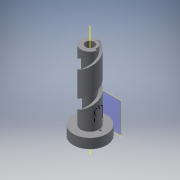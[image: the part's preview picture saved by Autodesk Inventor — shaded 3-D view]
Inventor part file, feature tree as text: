
AUTODESK INVENTOR PART (.ipt)
format: ipt  version: 2018 (Build 220112000, 112)  size: 228,864 bytes
history: native  units: mm
features: sketch x9, extrude x8, plane x1, other x1, helix x1
ambient origin geometry x8: Origin, YZ Plane, XZ Plane, XY Plane, X Axis, Y Axis, Z Axis, Center Point
bodies: Solid1 (feature_tree)
feature tree (20):
  extrude  "Extrusion1"  Depth=7.5mm
  extrude  "Extrusion2"  Depth=24.0mm
  extrude  "Extrusion3"  Depth=7.0mm
  extrude  "Extrusion5"  Depth=13.0mm
  plane  "Work Plane1"
  extrude  "Extrusion8"  Depth=6.5mm
  sketch  "Sketch9"  dims[d34=12.0mm d44=6.0mm]
  other  "Work Axis1"
  helix  "Coil2"  [1 undecoded]
  extrude  "Extrusión9"  Depth=6.0mm
  extrude  "Extrusión10"  Depth=5.0mm
  extrude  "Extrusión11"  Depth=7.0mm TaperAngle=0.0deg
  sketch  "Sketch1"  dims[d0=7.5mm d1=3.0mm]
  sketch  "Sketch2"  dims[d2=80.0mm d4=360.0deg d6=24.0mm]
  sketch  "Sketch3"  dims[d7=7.0mm d8=0.0mm d9=13.0mm]
  sketch  "Sketch5"  dims[d10=1.0mm d11=0.0mm d12=13.0mm]
  sketch  "Sketch8"  dims[d13=50.0mm d14=0.0mm d25=6.5mm d26=6.0mm d27=0.0mm]
  sketch  "Boceto13"  dims[d45=4.5mm d46=0.0mm d61=5.0mm]
  sketch  "Boceto14"  dims[d62=7.0mm]
  sketch  "Boceto15"  dims[d63=25.0mm d64=50.0mm d65=40.0mm d66=0.174533mm d67=90.0deg d68=90.0deg d69=0.0mm d70=0.0mm d72=7.0mm d73=0.0mm d74=2.0mm d75=0.0mm d76=7.5mm d77=7.5mm d78=6.0mm d79=6.0mm d80=1.5mm d81=1.5mm d82=1.5mm d83=1.5mm d84=7.0mm d85=0.0mm]
note: 1 required parameter value undecoded (feature->parameter linkage not recoverable at this tier; creation-order binding heuristic only, values carry confidence <= 0.55)
